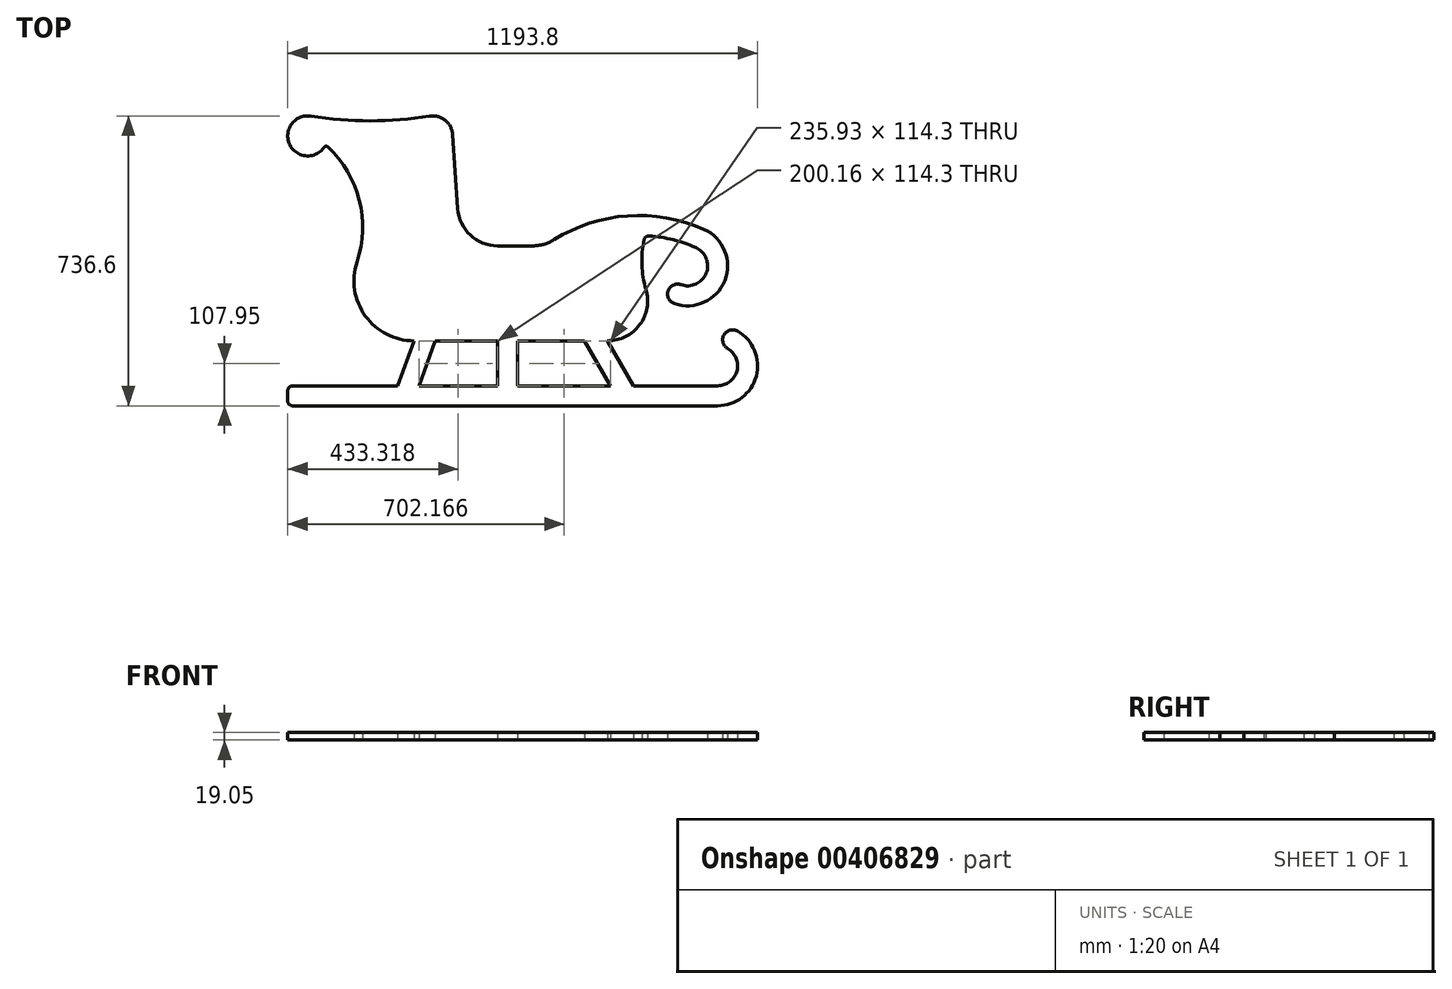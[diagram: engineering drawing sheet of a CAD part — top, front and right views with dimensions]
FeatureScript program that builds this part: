
annotation { "Feature Type Name" : "Feature", "Feature Type Description" : "" }
export const myFeature = defineFeature(function(context is Context, id is Id, definition is map)
    precondition{}
    {
        {
            var Q0;
            Q0=qCreatedBy(makeId("Top.planeOp"),FACE);
            var sketch = newSketch(context, id + "F0", { "sketchPlane" : qUnion([Q0])});
            skLineSegment(sketch, "E0.bottom", {"start": v(12.7, 0) * mm, "end": v(1092.2, 0) * mm});
            skLineSegment(sketch, "E0.top", {"start": v(0, 736.6) * mm, "end": v(1193.8, 736.6) * mm, "construction": true});
            skLineSegment(sketch, "E0.left", {"start": v(0, 0) * mm, "end": v(0, 736.6) * mm, "construction": true});
            skLineSegment(sketch, "E0.right", {"start": v(1193.8, 0) * mm, "end": v(1193.8, 736.6) * mm, "construction": true});
            skArc(sketch, "E1", {"start": v(176.19, 365.65) * mm, "mid": v(197.16, 228.37) * mm, "end": v(320.78, 165.1) * mm});
            skLineSegment(sketch, "E2", {"start": v(374.84, 165.1) * mm, "end": v(533.4, 165.1) * mm});
            skArc(sketch, "E3", {"start": v(812.8, 165.1) * mm, "mid": v(894.26, 205.98) * mm, "end": v(910.16, 295.73) * mm});
            skArc(sketch, "E4", {"start": v(176.19, 365.65) * mm, "mid": v(181.94, 522.57) * mm, "end": v(102.15, 657.8) * mm});
            skArc(sketch, "E5", {"start": v(905.3, 421.9) * mm, "mid": v(899.77, 358.5) * mm, "end": v(910.16, 295.73) * mm});
            skArc(sketch, "E6", {"start": v(982.13, 259.81) * mm, "mid": v(1110.35, 317.92) * mm, "end": v(1057.44, 448.36) * mm});
            skArc(sketch, "E7", {"start": v(58.88, 735.95) * mm, "mid": v(209.55, 723.9) * mm, "end": v(360.22, 735.95) * mm});
            skArc(sketch, "E8", {"start": v(58.88, 735.95) * mm, "mid": v(3.73, 666.69) * mm, "end": v(91.55, 655.47) * mm});
            skArc(sketch, "E9", {"start": v(418.98, 689.32) * mm, "mid": v(399.88, 725.59) * mm, "end": v(360.22, 735.95) * mm});
            skLineSegment(sketch, "E10", {"start": v(432.04, 500.97) * mm, "end": v(418.98, 689.32) * mm});
            skLineSegment(sketch, "E11", {"start": v(533.4, 406.4) * mm, "end": v(558.8, 406.4) * mm});
            skLineSegment(sketch, "E12", {"start": v(558.8, 406.4) * mm, "end": v(622.3, 406.4) * mm});
            skArc(sketch, "E13", {"start": v(1057.44, 448.36) * mm, "mid": v(863.5, 482.73) * mm, "end": v(676.18, 421.86) * mm});
            skArc(sketch, "E14", {"start": v(999.07, 307.7) * mm, "mid": v(966.65, 292.22) * mm, "end": v(982.13, 259.81) * mm});
            skArc(sketch, "E15.filletArc", {"start": v(622.3, 406.4) * mm, "mid": v(650.33, 410.34) * mm, "end": v(676.18, 421.86) * mm});
            skPoint(sketch, "E16.visualSharp", {"position": v(519.79, 406.4) * mm});
            skLineSegment(sketch, "E16.filletArc", {"start": v(558.8, 406.4) * mm, "end": v(558.8, 406.4) * mm});
            skPoint(sketch, "E17.visualSharp", {"position": v(438.6, 406.4) * mm});
            skArc(sketch, "E17.filletArc", {"start": v(432.04, 500.97) * mm, "mid": v(464.09, 433.71) * mm, "end": v(533.4, 406.4) * mm});
            skArc(sketch, "E18.0", {"start": v(999.07, 307.7) * mm, "mid": v(1063.18, 336.76) * mm, "end": v(1036.72, 401.98) * mm});
            skArc(sketch, "E18.1", {"start": v(1036.72, 401.98) * mm, "mid": v(978.99, 422.02) * mm, "end": v(918.67, 431.88) * mm});
            skArc(sketch, "E18.2", {"start": v(622.3, 355.6) * mm, "mid": v(664.34, 361.51) * mm, "end": v(703.11, 378.8) * mm, "construction": true});
            skLineSegment(sketch, "E18.3", {"start": v(558.8, 355.6) * mm, "end": v(622.3, 355.6) * mm, "construction": true});
            skLineSegment(sketch, "E18.4", {"start": v(558.8, 355.6) * mm, "end": v(558.8, 355.6) * mm});
            skLineSegment(sketch, "E18.5", {"start": v(533.4, 355.6) * mm, "end": v(558.8, 355.6) * mm, "construction": true});
            skArc(sketch, "E18.6", {"start": v(136.05, 675.8) * mm, "mid": v(226.07, 673.24) * mm, "end": v(315.96, 678.79) * mm, "construction": true});
            skLineSegment(sketch, "E18.8", {"start": v(381.37, 497.45) * mm, "end": v(372.05, 631.8) * mm, "construction": true});
            skArc(sketch, "E18.9", {"start": v(381.37, 497.45) * mm, "mid": v(429.43, 396.57) * mm, "end": v(533.4, 355.6) * mm, "construction": true});
            skPoint(sketch, "E19.visualSharp", {"position": v(101.14, 679) * mm});
            skArc(sketch, "E19.filletArc", {"start": v(92.88, 657.18) * mm, "mid": v(92.2, 656.33) * mm, "end": v(91.55, 655.47) * mm});
            skArc(sketch, "E20.filletArc", {"start": v(372.05, 631.8) * mm, "mid": v(354, 667.21) * mm, "end": v(315.96, 678.79) * mm, "construction": true});
            skLineSegment(sketch, "E21.0", {"start": v(12.7, 50.8) * mm, "end": v(279.18, 50.8) * mm});
            skLineSegment(sketch, "E22", {"start": v(0, 38.1) * mm, "end": v(0, 12.7) * mm});
            skPoint(sketch, "E23.visualSharp", {"position": v(0, 50.8) * mm});
            skArc(sketch, "E23.filletArc", {"start": v(12.7, 50.8) * mm, "mid": v(3.72, 47.08) * mm, "end": v(0, 38.1) * mm});
            skPoint(sketch, "E24.visualSharp", {"position": v(0, 0) * mm});
            skArc(sketch, "E24.filletArc", {"start": v(0, 12.7) * mm, "mid": v(3.72, 3.72) * mm, "end": v(12.7, 0) * mm});
            skArc(sketch, "E25", {"start": v(1092.2, 50.8) * mm, "mid": v(1141.27, 88.45) * mm, "end": v(1117.6, 145.6) * mm});
            skArc(sketch, "E26", {"start": v(1143, 189.59) * mm, "mid": v(1108.3, 180.3) * mm, "end": v(1117.6, 145.6) * mm});
            skArc(sketch, "E27", {"start": v(1092.2, 0) * mm, "mid": v(1190.34, 75.3) * mm, "end": v(1143, 189.59) * mm});
            skLineSegment(sketch, "E28", {"start": v(320.78, 165.1) * mm, "end": v(279.18, 50.8) * mm});
            skLineSegment(sketch, "E29", {"start": v(812.8, 165.1) * mm, "end": v(878.8, 50.8) * mm});
            skLineSegment(sketch, "E30", {"start": v(584.2, 165.1) * mm, "end": v(584.2, 50.8) * mm});
            skLineSegment(sketch, "E31.0", {"start": v(374.84, 165.1) * mm, "end": v(333.24, 50.8) * mm});
            skLineSegment(sketch, "E32.0", {"start": v(533.4, 165.1) * mm, "end": v(533.4, 50.8) * mm});
            skLineSegment(sketch, "E33.0", {"start": v(754.14, 165.1) * mm, "end": v(820.13, 50.8) * mm});
            skLineSegment(sketch, "E34.trimOffspring", {"start": v(878.8, 50.8) * mm, "end": v(1092.2, 50.8) * mm});
            skLineSegment(sketch, "E35.trimOffspring", {"start": v(584.2, 50.8) * mm, "end": v(820.13, 50.8) * mm});
            skLineSegment(sketch, "E36.trimOffspring", {"start": v(584.2, 165.1) * mm, "end": v(754.14, 165.1) * mm});
            skLineSegment(sketch, "E37.trimOffspring", {"start": v(333.24, 50.8) * mm, "end": v(533.4, 50.8) * mm});
            skArc(sketch, "E38.filletArc", {"start": v(102.15, 657.8) * mm, "mid": v(97.38, 659.51) * mm, "end": v(92.88, 657.18) * mm});
            skArc(sketch, "E39", {"start": v(849.37, 430.38) * mm, "mid": v(773.4, 412.66) * mm, "end": v(703.11, 378.8) * mm, "construction": true});
            skPoint(sketch, "E40.visualSharp", {"position": v(907.83, 432.54) * mm});
            skArc(sketch, "E40.filletArc", {"start": v(918.67, 431.88) * mm, "mid": v(910.11, 429.4) * mm, "end": v(905.3, 421.9) * mm});
            skSolve(sketch);
        }
        {
            var Q0;
            Q0 = qSketchRegion(id + "F0", true);
            extrude(context, id + "F1", {"entities" : qUnion([Q0]), "depth" : 19.05 * mm});
        }
    });
